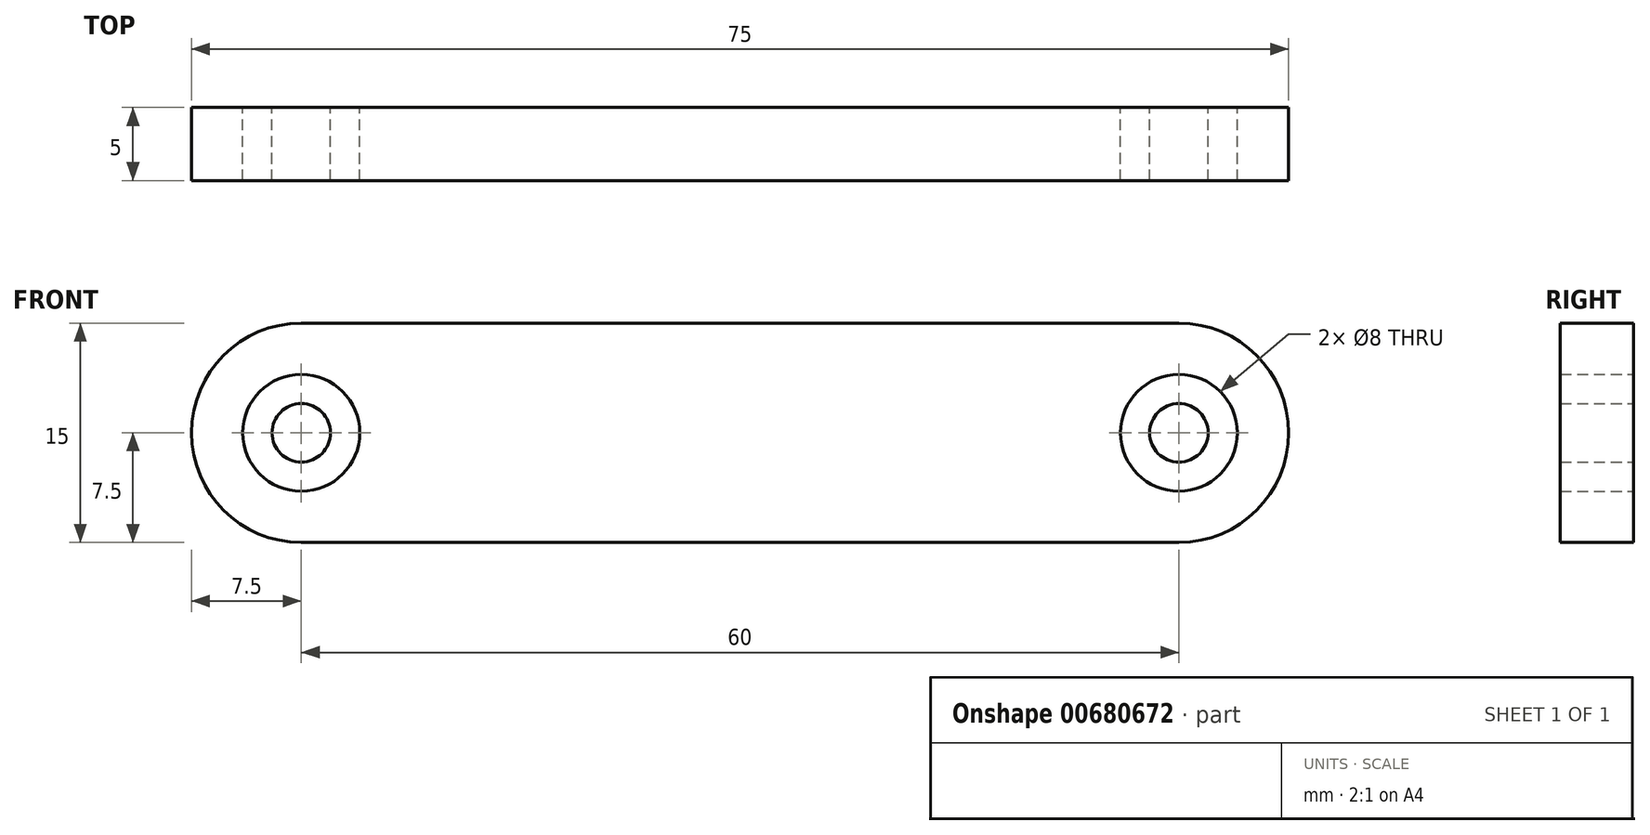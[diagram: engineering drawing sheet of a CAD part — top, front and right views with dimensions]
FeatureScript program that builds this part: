
annotation { "Feature Type Name" : "Feature", "Feature Type Description" : "" }
export const myFeature = defineFeature(function(context is Context, id is Id, definition is map)
    precondition{}
    {
        {
            var Q0;
            Q0=qCreatedBy(makeId("Front.planeOp"),FACE);
            var sketch = newSketch(context, id + "F0", { "sketchPlane" : qUnion([Q0])});
            skArc(sketch, "E0", {"start": v(0, 7.5) * mm, "mid": v(-7.5, 0) * mm, "end": v(0, -7.5) * mm});
            skCircle(sketch, "E1", {"center": v(0, 0) * mm, "radius": 4 * mm});
            skCircle(sketch, "E2", {"center": v(0, 0) * mm, "radius": 2 * mm});
            skLineSegment(sketch, "E3", {"start": v(0, 7.5) * mm, "end": v(60, 7.5) * mm});
            skArc(sketch, "E4", {"start": v(60, -7.5) * mm, "mid": v(67.5, 0) * mm, "end": v(60, 7.5) * mm});
            skCircle(sketch, "E5", {"center": v(60, 0) * mm, "radius": 4 * mm});
            skCircle(sketch, "E6", {"center": v(60, 0) * mm, "radius": 2 * mm});
            skLineSegment(sketch, "E7", {"start": v(0, -7.5) * mm, "end": v(60, -7.5) * mm});
            skSolve(sketch);
        }
        {
            var Q0;
            Q0=makeQuery(id+"F0.imprint","IMPRINT",FACE,{"disambiguationData":[TD([[makeQuery(id+"F0.imprint","IMPRINT",EDGE,{"derivedFrom":sQuery(id+"F0.wireOp",EDGE,"E2")}),1.0]])]});
            var Q1;
            Q1=makeQuery(id+"F0.imprint","IMPRINT",FACE,{"disambiguationData":[TD([[makeQuery(id+"F0.imprint","IMPRINT",EDGE,{"derivedFrom":sQuery(id+"F0.wireOp",EDGE,"E6")}),1.0]])]});
            var Q2;
            Q2=makeQuery(id+"F0.imprint","IMPRINT",FACE,{"disambiguationData":[TD([[makeQuery(id+"F0.imprint","IMPRINT",EDGE,{"derivedFrom":sQuery(id+"F0.wireOp",EDGE,"E0")}),1.0]])]});
            extrude(context, id + "F1", {"entities" : qUnion([Q0, Q1, Q2]), "depth" : 5 * mm, "offsetDistance" : 25.4 * mm});
        }
    });
